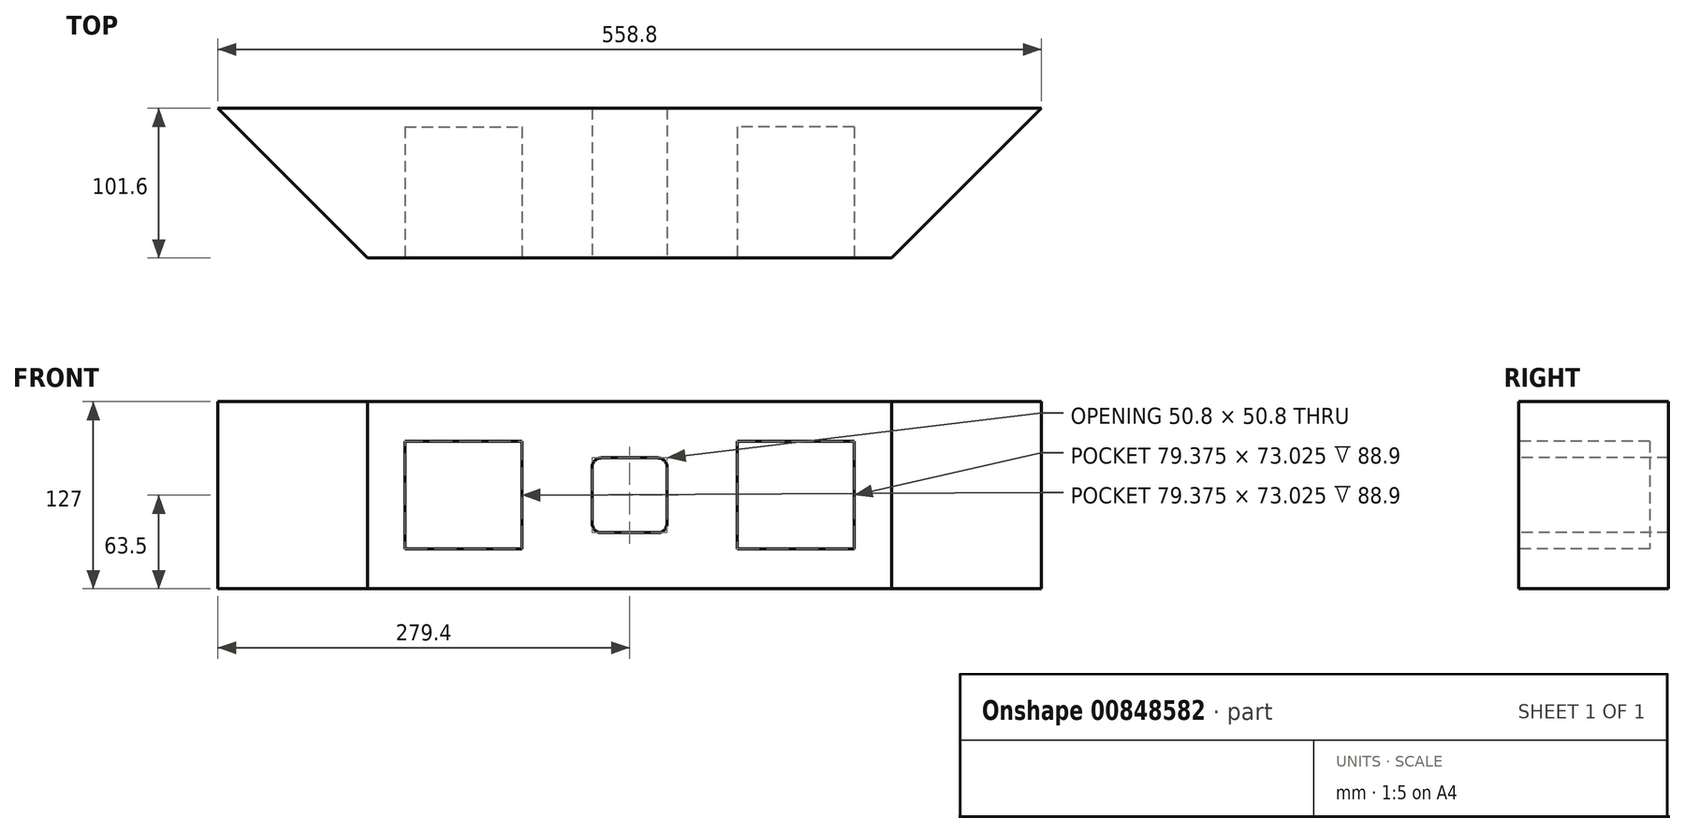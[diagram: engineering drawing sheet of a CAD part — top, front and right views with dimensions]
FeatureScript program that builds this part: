
annotation { "Feature Type Name" : "Feature", "Feature Type Description" : "" }
export const myFeature = defineFeature(function(context is Context, id is Id, definition is map)
    precondition{}
    {
        {
            var Q0;
            Q0=qCreatedBy(makeId("Top.planeOp"),FACE);
            var sketch = newSketch(context, id + "F0", { "sketchPlane" : qUnion([Q0])});
            skLineSegment(sketch, "E0.bottom", {"start": v(-177.8, 0) * mm, "end": v(177.8, 0) * mm});
            skLineSegment(sketch, "E0.top", {"start": v(-177.8, -101.6) * mm, "end": v(177.8, -101.6) * mm});
            skLineSegment(sketch, "E1", {"start": v(-279.4, 0) * mm, "end": v(-177.8, -101.6) * mm});
            skLineSegment(sketch, "E2", {"start": v(-177.8, 0) * mm, "end": v(-279.4, 0) * mm});
            skLineSegment(sketch, "E3", {"start": v(177.8, 0) * mm, "end": v(279.4, 0) * mm});
            skLineSegment(sketch, "E4", {"start": v(279.4, 0) * mm, "end": v(177.8, -101.6) * mm});
            skSolve(sketch);
        }
        {
            var Q0;
            Q0 = qSketchRegion(id + "F0", true);
            extrude(context, id + "F1", {"entities" : qUnion([Q0]), "depth" : 127 * mm, "offsetDistance" : 25.4 * mm});
        }
        {
            var Q0;
            Q0=makeQuery(id+"F1.opExtrude","SWEPT_FACE",FACE,{"disambiguationData":[OSD([sQuery(id+"F0.wireOp",EDGE,"E0.top")])]});
            var sketch = newSketch(context, id + "F2", { "sketchPlane" : qUnion([Q0])});
            skLineSegment(sketch, "E5.bottom", {"start": v(-19.05, 88.9) * mm, "end": v(19.05, 88.9) * mm});
            skLineSegment(sketch, "E5.top", {"start": v(-19.05, 38.1) * mm, "end": v(19.05, 38.1) * mm});
            skLineSegment(sketch, "E5.left", {"start": v(-25.4, 82.55) * mm, "end": v(-25.4, 44.45) * mm});
            skLineSegment(sketch, "E5.right", {"start": v(25.4, 82.55) * mm, "end": v(25.4, 44.45) * mm});
            skPoint(sketch, "E6.visualSharp", {"position": v(-25.4, 88.9) * mm});
            skArc(sketch, "E6.filletArc", {"start": v(-19.05, 88.9) * mm, "mid": v(-23.54, 87.04) * mm, "end": v(-25.4, 82.55) * mm});
            skPoint(sketch, "E7.visualSharp", {"position": v(25.4, 88.9) * mm});
            skArc(sketch, "E7.filletArc", {"start": v(25.4, 82.55) * mm, "mid": v(23.54, 87.04) * mm, "end": v(19.05, 88.9) * mm});
            skPoint(sketch, "E8.visualSharp", {"position": v(25.4, 38.1) * mm});
            skArc(sketch, "E8.filletArc", {"start": v(19.05, 38.1) * mm, "mid": v(23.54, 39.96) * mm, "end": v(25.4, 44.45) * mm});
            skPoint(sketch, "E9.visualSharp", {"position": v(-25.4, 38.1) * mm});
            skArc(sketch, "E9.filletArc", {"start": v(-25.4, 44.45) * mm, "mid": v(-23.54, 39.96) * mm, "end": v(-19.05, 38.1) * mm});
            skSolve(sketch);
        }
        {
            var Q0;
            Q0=makeQuery(id+"F2.imprint","IMPRINT",FACE,{"disambiguationData":[TD([[makeQuery(id+"F2.imprint","IMPRINT",EDGE,{"derivedFrom":sQuery(id+"F2.wireOp",EDGE,"E5.bottom")}),-1.0]])]});
            extrude(context, id + "F3", {"entities" : qUnion([Q0]), "operationType" : NewBodyOperationType.REMOVE, "endBound" : BoundingType.THROUGH_ALL, "oppositeDirection" : true, "depth" : 25.4 * mm, "offsetDistance" : 25.4 * mm});
        }
        {
            var Q0;
            Q0=makeQuery(id+"F1.opExtrude","SWEPT_FACE",FACE,{"disambiguationData":[OSD([sQuery(id+"F0.wireOp",EDGE,"E0.top")])]});
            var sketch = newSketch(context, id + "F4", { "sketchPlane" : qUnion([Q0])});
            skLineSegment(sketch, "E10.bottom", {"start": v(-152.4, 100.01) * mm, "end": v(-73.03, 100.01) * mm});
            skLineSegment(sketch, "E10.top", {"start": v(-152.4, 26.99) * mm, "end": v(-73.03, 26.99) * mm});
            skLineSegment(sketch, "E10.left", {"start": v(-152.4, 100.01) * mm, "end": v(-152.4, 26.99) * mm});
            skLineSegment(sketch, "E10.right", {"start": v(-73.03, 100.01) * mm, "end": v(-73.03, 26.99) * mm});
            skLineSegment(sketch, "E11", {"start": v(166.81, 63.5) * mm, "end": v(-165.8, 63.5) * mm});
            skPoint(sketch, "E11.startSnap0", {"position": v(-25.4, 63.5) * mm});
            skPoint(sketch, "E12", {"position": v(-73.03, 63.5) * mm});
            skLineSegment(sketch, "E13.MirrorCS", {"start": v(152.4, 100.01) * mm, "end": v(73.03, 100.01) * mm});
            skLineSegment(sketch, "E14.MirrorCS", {"start": v(73.03, 100.01) * mm, "end": v(73.03, 26.99) * mm});
            skLineSegment(sketch, "E15.MirrorCS", {"start": v(152.4, 26.99) * mm, "end": v(73.03, 26.99) * mm});
            skLineSegment(sketch, "E16.MirrorCS", {"start": v(152.4, 100.01) * mm, "end": v(152.4, 26.99) * mm});
            skSolve(sketch);
        }
        {
            var Q0;
            {var subQ0=sQuery(id+"F4.wireOp",EDGE,"8RVBPzka-A6kl-foFp-XU1Q-PGrzug00MHZm.bottom");Q0=makeQuery(id+"F4.imprint","IMPRINT",FACE,{"disambiguationData":[TD([[makeQuery(id+"F4.imprint","IMPRINT",EDGE,{"derivedFrom":subQ0}),-1.0]])]});}
            var Q1;
            {var subQ0=sQuery(id+"F4.wireOp",EDGE,"8RVBPzka-A6kl-foFp-XU1Q-PGrzug00MHZm.top");Q1=makeQuery(id+"F4.imprint","IMPRINT",FACE,{"disambiguationData":[TD([[makeQuery(id+"F4.imprint","IMPRINT",EDGE,{"derivedFrom":subQ0}),1.0]])]});}
            var Q2;
            {var subQ0=sQuery(id+"F4.wireOp",EDGE,"E10.top");Q2=makeQuery(id+"F4.imprint","IMPRINT",FACE,{"disambiguationData":[TD([[makeQuery(id+"F4.imprint","IMPRINT",EDGE,{"derivedFrom":subQ0}),1.0]])]});}
            var Q3;
            {var subQ0=sQuery(id+"F4.wireOp",EDGE,"E10.bottom");Q3=makeQuery(id+"F4.imprint","IMPRINT",FACE,{"disambiguationData":[TD([[makeQuery(id+"F4.imprint","IMPRINT",EDGE,{"derivedFrom":subQ0}),-1.0]])]});}
            var Q4;
            {var subQ5=sQuery(id+"F4.wireOp",EDGE,"E13.MirrorCS");Q4=makeQuery(id+"F4.imprint","IMPRINT",FACE,{"disambiguationData":[TD([[makeQuery(id+"F4.imprint","IMPRINT",EDGE,{"derivedFrom":subQ5}),1.0]])]});}
            var Q5;
            {var subQ5=sQuery(id+"F4.wireOp",EDGE,"E15.MirrorCS");Q5=makeQuery(id+"F4.imprint","IMPRINT",FACE,{"disambiguationData":[TD([[makeQuery(id+"F4.imprint","IMPRINT",EDGE,{"derivedFrom":subQ5}),-1.0]])]});}
            extrude(context, id + "F5", {"entities" : qUnion([Q0, Q1, Q2, Q3, Q4, Q5]), "operationType" : NewBodyOperationType.REMOVE, "oppositeDirection" : true, "depth" : 88.9 * mm, "offsetDistance" : 25.4 * mm});
        }
    });
